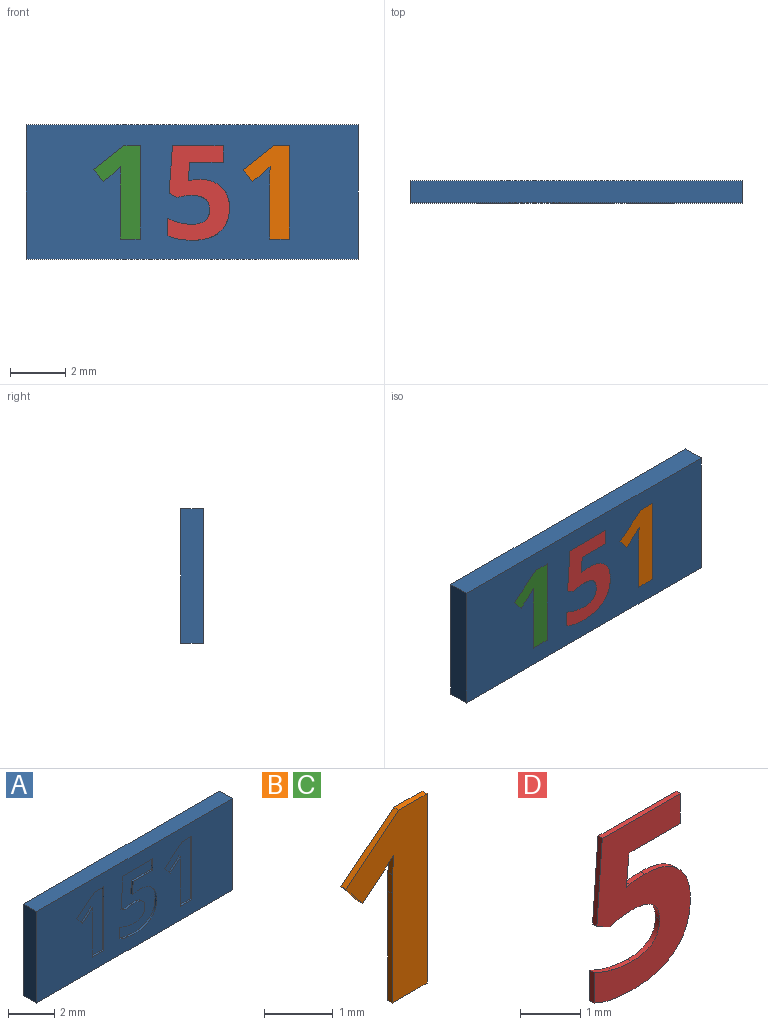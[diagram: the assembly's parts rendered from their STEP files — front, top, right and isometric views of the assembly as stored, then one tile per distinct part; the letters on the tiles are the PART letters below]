
ASSEMBLY  parts=4 mates=3
PART A: 49 faces, bbox 12x0.8x4.9 mm
  f0: plane 12x4.85mm, normal (0,-1,0), area 47.8mm2, adj f1,f2,f3,f4,f6,f7,f8,f9
  f1: plane 12x0.8mm, normal (0,0,-1), area 9.6mm2, adj f0,f2,f4,f5
  f2: plane 4.85x0.8mm, normal (1,0,0), area 3.9mm2, adj f0,f1,f3,f5
  f3: plane 12x0.8mm, normal (0,0,1), area 9.6mm2, adj f0,f2,f4,f5
  f4: plane 4.85x0.8mm, normal (-1,0,0), area 3.9mm2, adj f0,f1,f3,f5
  f5: plane 12x4.85mm, normal (0,1,0), area 58.2mm2, adj f1,f2,f3,f4
  f6: plane 3.37x0.1mm, normal (-1,0,0), area 0.3mm2, adj f0,f7,f15,f16
  f7: plane 0.59x0.1mm, normal (0,0,-1), area 0.1mm2, adj f0,f6,f8,f16
  f8: plane 1.09x0.86mm, normal (0.62,0,-0.78), area 0.1mm2, adj f0,f7,f9,f16
  f9: plane 0.43x0.34mm, normal (0.78,0,0.63), area 0.1mm2, adj f0,f8,f10,f16
  f10: plane 0.39x0.31mm, normal (-0.63,0,0.78), area 0mm2, adj f0,f9,f11,f16
  f11: extruded ~0.25x0.23mm, area 0mm2, adj f0,f10,f12,f16
  f12: plane 0.35x0.1mm, normal (1,0,-0.03), area 0mm2, adj f0,f11,f13,f16
  f13: plane 0.32x0.1mm, normal (1,0,-0.02), area 0mm2, adj f0,f12,f14,f16
  f14: plane 1.95x0.1mm, normal (1,0,0), area 0.2mm2, adj f0,f13,f15,f16
  f15: plane 0.71x0.1mm, normal (0,0,1), area 0.1mm2, adj f0,f6,f14,f16
  f16: plane 3.37x1.67mm, normal (0,-1,0), area 2.9mm2, adj f6,f7,f8,f9,f10,f11,f12,f13
  f17: extruded ~0.35x0.1mm, area 0mm2, adj f0,f18,f36,f37
  f18: plane 0.1x0.08mm, normal (0.2,0,-0.98), area 0mm2, adj f0,f17,f19,f37
  f19: plane 0.66x0.1mm, normal (-1,0,0.09), area 0.1mm2, adj f0,f18,f20,f37
  f20: plane 1.2x0.1mm, normal (0,0,1), area 0.1mm2, adj f0,f19,f21,f37
  f21: plane 0.6x0.1mm, normal (-1,0,0), area 0.1mm2, adj f0,f20,f22,f37
  f22: plane 1.83x0.1mm, normal (0,0,-1), area 0.2mm2, adj f0,f21,f23,f37
  f23: plane 1.72x0.13mm, normal (1,0,-0.07), area 0.2mm2, adj f0,f22,f24,f37
  f24: plane 0.28x0.15mm, normal (0.47,0,0.88), area 0mm2, adj f0,f23,f25,f37
  f25: extruded ~0.24x0.1mm, area 0mm2, adj f0,f24,f26,f37
  f26: extruded ~0.27x0.1mm, area 0mm2, adj f0,f25,f27,f37
  f27: extruded ~0.68x0.51mm, area 0.1mm2, adj f0,f26,f28,f37
  f28: extruded ~0.65x0.54mm, area 0.1mm2, adj f0,f27,f29,f37
  f29: extruded ~0.46x0.1mm, area 0mm2, adj f0,f28,f30,f37
  f30: extruded ~0.42x0.16mm, area 0mm2, adj f0,f29,f31,f37
  f31: plane 0.62x0.1mm, normal (1,0,0), area 0.1mm2, adj f0,f30,f32,f37
  f32: extruded ~0.91x0.18mm, area 0.1mm2, adj f0,f31,f33,f37
  f33: extruded ~1x0.3mm, area 0.1mm2, adj f0,f32,f34,f37
  f34: extruded ~0.87x0.35mm, area 0.1mm2, adj f0,f33,f35,f37
  f35: extruded ~0.75x0.29mm, area 0.1mm2, adj f0,f34,f36,f37
  f36: extruded ~0.78x0.27mm, area 0.1mm2, adj f0,f17,f35,f37
  f37: plane 3.42x2.25mm, normal (0,-1,0), area 4.5mm2, adj f17,f18,f19,f20,f21,f22,f23,f24
  f38: plane 3.37x0.1mm, normal (-1,0,0), area 0.3mm2, adj f0,f39,f47,f48
  f39: plane 0.59x0.1mm, normal (0,0,-1), area 0.1mm2, adj f0,f38,f40,f48
  f40: plane 1.09x0.86mm, normal (0.62,0,-0.78), area 0.1mm2, adj f0,f39,f41,f48
  f41: plane 0.43x0.34mm, normal (0.78,0,0.63), area 0.1mm2, adj f0,f40,f42,f48
  f42: plane 0.39x0.31mm, normal (-0.63,0,0.78), area 0mm2, adj f0,f41,f43,f48
  f43: extruded ~0.25x0.23mm, area 0mm2, adj f0,f42,f44,f48
  f44: plane 0.35x0.1mm, normal (1,0,-0.03), area 0mm2, adj f0,f43,f45,f48
  f45: plane 0.32x0.1mm, normal (1,0,-0.02), area 0mm2, adj f0,f44,f46,f48
  f46: plane 1.95x0.1mm, normal (1,0,0), area 0.2mm2, adj f0,f45,f47,f48
  f47: plane 0.71x0.1mm, normal (0,0,1), area 0.1mm2, adj f0,f38,f46,f48
  f48: plane 3.37x1.67mm, normal (0,-1,0), area 2.9mm2, adj f38,f39,f40,f41,f42,f43,f44,f45
PART B: 12 faces, bbox 1.7x0.1x3.4 mm
  f0: plane 3.37x1.67mm, normal (0,-1,0), area 2.9mm2, adj f1,f2,f3,f4,f5,f6,f7,f9
  f1: plane 0.59x0.1mm, normal (0,0,1), area 0.1mm2, adj f0,f2,f8,f10
  f2: plane 1.09x0.86mm, normal (-0.62,0,0.78), area 0.1mm2, adj f0,f1,f3,f8
  f3: plane 0.43x0.34mm, normal (-0.78,0,-0.63), area 0.1mm2, adj f0,f2,f4,f8
  f4: plane 0.39x0.31mm, normal (0.63,0,-0.78), area 0mm2, adj f0,f3,f5,f8
  f5: extruded ~0.25x0.23mm, area 0mm2, adj f0,f4,f6,f8
  f6: plane 0.35x0.1mm, normal (-1,0,0.03), area 0mm2, adj f0,f5,f7,f8
  f7: plane 0.32x0.1mm, normal (-1,0,0.02), area 0mm2, adj f0,f6,f8,f9
  f8: plane 3.37x1.67mm, normal (0,1,0), area 2.9mm2, adj f1,f2,f3,f4,f5,f6,f7,f9
  f9: plane 1.95x0.1mm, normal (-1,0,0), area 0.2mm2, adj f0,f7,f8,f11
  f10: plane 3.37x0.1mm, normal (1,0,0), area 0.3mm2, adj f0,f1,f8,f11
  f11: plane 0.71x0.1mm, normal (0,0,-1), area 0.1mm2, adj f0,f8,f9,f10
PART C: same geometry as B
PART D: 22 faces, bbox 2.3x0.1x3.4 mm
  f0: plane 3.42x2.25mm, normal (0,-1,0), area 4.5mm2, adj f1,f2,f3,f4,f5,f6,f7,f8
  f1: plane 0.1x0.08mm, normal (-0.2,0,0.98), area 0mm2, adj f0,f2,f18,f20
  f2: plane 0.66x0.1mm, normal (1,0,-0.09), area 0.1mm2, adj f0,f1,f3,f18
  f3: plane 1.2x0.1mm, normal (0,0,-1), area 0.1mm2, adj f0,f2,f4,f18
  f4: plane 0.6x0.1mm, normal (1,0,0), area 0.1mm2, adj f0,f3,f5,f18
  f5: plane 1.83x0.1mm, normal (0,0,1), area 0.2mm2, adj f0,f4,f6,f18
  f6: plane 1.72x0.13mm, normal (-1,0,0.07), area 0.2mm2, adj f0,f5,f7,f18
  f7: plane 0.28x0.15mm, normal (-0.47,0,-0.88), area 0mm2, adj f0,f6,f8,f18
  f8: extruded ~0.24x0.1mm, area 0mm2, adj f0,f7,f9,f18
  f9: extruded ~0.27x0.1mm, area 0mm2, adj f0,f8,f10,f18
  f10: extruded ~0.68x0.51mm, area 0.1mm2, adj f0,f9,f11,f18
  f11: extruded ~0.65x0.54mm, area 0.1mm2, adj f0,f10,f12,f18
  f12: extruded ~0.46x0.1mm, area 0mm2, adj f0,f11,f13,f18
  f13: extruded ~0.42x0.16mm, area 0mm2, adj f0,f12,f14,f18
  f14: plane 0.62x0.1mm, normal (-1,0,0), area 0.1mm2, adj f0,f13,f15,f18
  f15: extruded ~0.91x0.18mm, area 0.1mm2, adj f0,f14,f16,f18
  f16: extruded ~1x0.3mm, area 0.1mm2, adj f0,f15,f17,f18
  f17: extruded ~0.87x0.35mm, area 0.1mm2, adj f0,f16,f18,f19
  f18: plane 3.42x2.25mm, normal (0,1,0), area 4.5mm2, adj f1,f2,f3,f4,f5,f6,f7,f8
  f19: extruded ~0.75x0.29mm, area 0.1mm2, adj f0,f17,f18,f21
  f20: extruded ~0.35x0.1mm, area 0mm2, adj f0,f1,f18,f21
  f21: extruded ~0.78x0.27mm, area 0.1mm2, adj f0,f18,f19,f20
PLACE A t=(0.02,0.39,-0.03)mm
PLACE B t=(1.14,0.39,-0.03)mm
PLACE C t=(-4.25,0.39,-0.03)mm
PLACE D t=(-1.28,0.39,-0.03)mm
MATE fastened B.f0 <-> A.f0  axis (0,-1,0) through (2.82,-0.41,-1.73)mm
MATE fastened D.f0 <-> A.f0  axis (0,-1,0) through (-0.88,-0.41,-1.59)mm
MATE fastened C.f0 <-> A.f0  axis (0,-1,0) through (-2.57,-0.41,-1.73)mm
